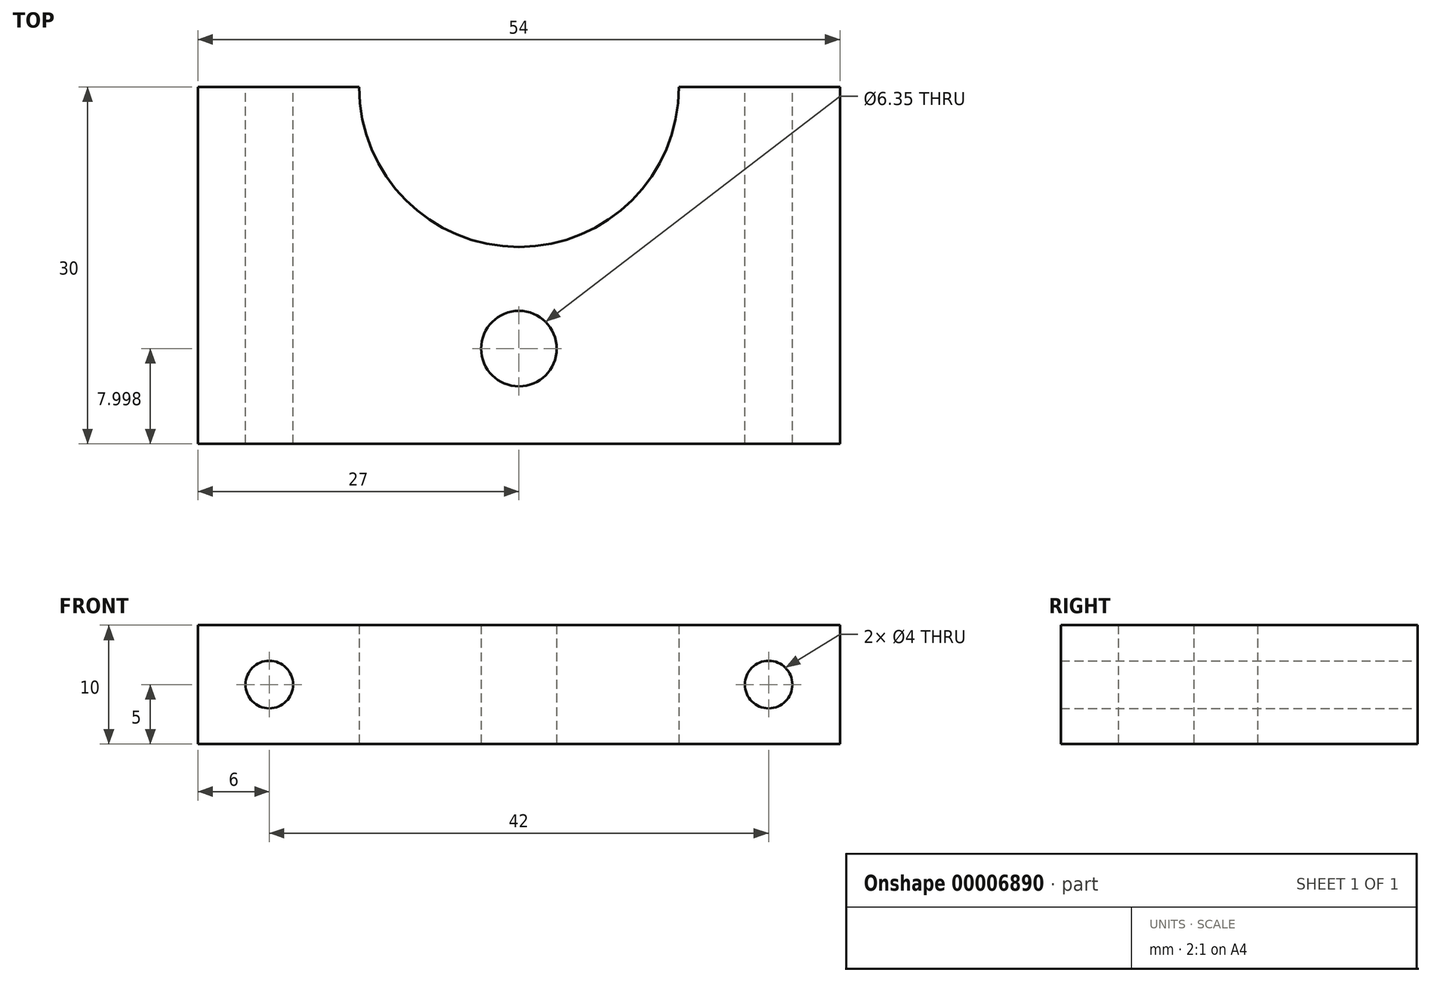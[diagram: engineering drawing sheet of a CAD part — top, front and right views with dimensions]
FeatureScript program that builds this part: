
annotation { "Feature Type Name" : "Feature", "Feature Type Description" : "" }
export const myFeature = defineFeature(function(context is Context, id is Id, definition is map)
    precondition{}
    {
        {
            var Q0;
            Q0=qCreatedBy(makeId("Top.planeOp"),FACE);
            var sketch = newSketch(context, id + "F0", { "sketchPlane" : qUnion([Q0])});
            skLineSegment(sketch, "E0.bottom", {"start": v(-27, -6.56) * mm, "end": v(-13.45, -6.56) * mm});
            skLineSegment(sketch, "E0.top", {"start": v(-27, -36.56) * mm, "end": v(27, -36.56) * mm});
            skLineSegment(sketch, "E0.left", {"start": v(-27, -6.56) * mm, "end": v(-27, -36.56) * mm});
            skLineSegment(sketch, "E0.right", {"start": v(27, -6.56) * mm, "end": v(27, -36.56) * mm});
            skArc(sketch, "E1", {"start": v(-13.45, -6.56) * mm, "mid": v(0, -20.01) * mm, "end": v(13.45, -6.56) * mm});
            skLineSegment(sketch, "E2.trimOffspring", {"start": v(13.45, -6.56) * mm, "end": v(27, -6.56) * mm});
            skCircle(sketch, "E3", {"center": v(0, -28.56) * mm, "radius": 3.17 * mm});
            skSolve(sketch);
        }
        {
            var Q0;
            Q0=qSketchRegion(id+"F0",true);
            var Q1;
            Q1=makeQuery(id+"F0.imprint","IMPRINT",FACE,{"disambiguationData":[TD([[makeQuery(id+"F0.imprint","IMPRINT",EDGE,{"derivedFrom":sQuery(id+"F0.wireOp",EDGE,"E0.bottom")}),-1.0]])]});
            extrude(context, id + "F1", {"entities" : qUnion([Q0, Q1]), "depth" : 10 * mm});
        }
        {
            var Q0;
            Q0=makeQuery(id+"F1.opExtrude","SWEPT_FACE",FACE,{"disambiguationData":[OSD([sQuery(id+"F0.wireOp",EDGE,"E2.trimOffspring")])]});
            var sketch = newSketch(context, id + "F2", { "sketchPlane" : qUnion([Q0])});
            skLineSegment(sketch, "E4", {"start": v(-21, 10) * mm, "end": v(-21, 0) * mm, "construction": true});
            skLineSegment(sketch, "E5", {"start": v(-27, 5) * mm, "end": v(-13.45, 5) * mm, "construction": true});
            skCircle(sketch, "E6", {"center": v(-21, 5) * mm, "radius": 2 * mm});
            skSolve(sketch);
        }
        {
            var Q0;
            Q0=qSketchRegion(id+"F2",true);
            extrude(context, id + "F3", {"entities" : qUnion([Q0]), "operationType" : NewBodyOperationType.REMOVE, "endBound" : BoundingType.THROUGH_ALL, "oppositeDirection" : true, "depth" : 25 * mm});
        }
        {
            var Q0;
            Q0=makeQuery(id+"F1.opExtrude","SWEPT_FACE",FACE,{"disambiguationData":[OSD([sQuery(id+"F0.wireOp",EDGE,"E0.bottom")])]});
            var sketch = newSketch(context, id + "F4", { "sketchPlane" : qUnion([Q0])});
            skLineSegment(sketch, "E7", {"start": v(21, 10) * mm, "end": v(21, 0) * mm, "construction": true});
            skLineSegment(sketch, "E8", {"start": v(27, 5) * mm, "end": v(13.45, 5) * mm, "construction": true});
            skCircle(sketch, "E9", {"center": v(21, 5) * mm, "radius": 2 * mm});
            skSolve(sketch);
        }
        {
            var Q0;
            Q0=qSketchRegion(id+"F4",true);
            extrude(context, id + "F5", {"entities" : qUnion([Q0]), "operationType" : NewBodyOperationType.REMOVE, "endBound" : BoundingType.THROUGH_ALL, "oppositeDirection" : true, "depth" : 25 * mm});
        }
    });
